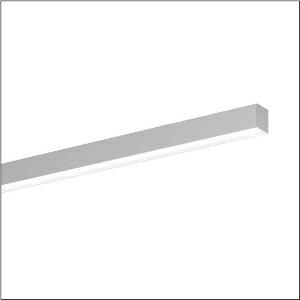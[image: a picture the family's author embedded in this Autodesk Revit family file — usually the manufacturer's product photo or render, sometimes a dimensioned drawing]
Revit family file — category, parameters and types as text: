
# Revit family: silica_r__21_51mx23da44sb_489f
name_source: partatom
category: Lighting Fixtures
units: mm (PartAtom-declared; Revit-internal decimal feet)

## family parameters
Cut with Voids When Loaded = No
Host = Face
Light Source = No
Part Type = Normal
Room Calculation Point = No
Round Connector Dimension = Use Diameter
Shared = No

## types (1)
- --- (1 x LED, 3280 lm, 22.4 W, 4000K)
    Apparent Load = 22 VA
    CIE Flux Codes = 78 96 99 100 100
    Color Rendering = 80
    Color Temperature = 4000K
    Default Elevation = 1800 mm
    Description = Silica® 21, office luminaire, primary optical cover: prismatic diffuser, of PMMA, CAT 2 (L<= 3000cd/m²), light emission: direct distribution, primary light characteristic: symmetric, installation type: surface-mounted, LED, rated luminous flux: 3.280lm, luminous efficacy: 146lm/W, light colour: 840, colour temperature: 4000K, with terminal, 3+2-pole, max. 2.5mm², mains connection: 220..240V, AC, 50/60Hz, rated input power: 22.4W, luminaire housing, of aluminium, metallic grey (RAL 9006), length: 1.204mm, width: 53mm, height: 53mm, protection rating (complete): IP20, insulation class (complete): insulation class I (protective earthing), certification: CE, permissible operating ambient temperature: 0..+35°C, standard: EN 50419, packaging unit: 1 piece
    Height = 0 mm  [stored 0 ft]
    Lamp = 1 x LED
    Lamp Light Flux = 3280 lm
    Lamp Power = 22.4 W
    Lamp count = 1
    Length = 1204 mm
    Luminous efficacy = 146 lm/W
    Manufacturer = Siteco
    ModVariant = No
    Model = 51MX23DA44SB
    Mounting Place = Ceiling
    Mounting Type = Recessed
    Number of Poles = 1
    OnlyDefault = Yes
    Power Factor = 1
    Product Name = Silica® 21
    Product group = office luminaire | ceiling recessed
    ProductGroupID = 400
    Protection Class = Protection class I
    Protection Degree = IP 20
    RLX_Detail_Level = 1
    RLX_Emergency_Light_Flux = 0 lm
    RLX_Emergency_Type = 0
    RLX_Emergency_Type_DB = No
    RlxData = <blob elided: 21125 chars, md5=fac3dd9b>
    Socket = socket
    Standby Power = 0 W
    System Light Flux = 3280 lm
    System Power = 22 W
    Type Comments = factory setting: luminous flux: 100 % | dim-lin: 254 | 323 mA
    Type Image = l_1335933.jpg
    URL = http://relux.com
    VarID = @adj_088589
    Voltage = 0 V
    Weight = 0.00 kg
    Width = 53 mm

note: [stored X ft] marks values corroborated as IEEE doubles in the binary element streams (Revit-internal decimal feet)

## geometry (parser evidence)
native form markers: Blend x4, Sweep x14
no freeform markers — native parametric forms only
